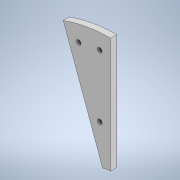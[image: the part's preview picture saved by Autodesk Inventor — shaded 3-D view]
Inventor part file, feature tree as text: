
AUTODESK INVENTOR PART (.ipt)
format: ipt  version: 2020.3 (Build 243373000, 373)  size: 159,232 bytes
history: native  units: mm
features: extrude x4, sketch x3, pattern_circular x1
ambient origin geometry x8: Origin, YZ Plane, XZ Plane, XY Plane, X Axis, Y Axis, Z Axis, Center Point
bodies: Solid1 (feature_tree)
feature tree (8):
  extrude  "Extrusion1"  Depth=90.0mm
  extrude  "Extrusion2"  Depth=4.0mm
  pattern_circular  "Circular Pattern1"  Count=8  [1 undecoded]
  extrude  "Extrusion4"  TaperAngle=15.0deg  [1 undecoded]
  extrude  "Extrusion5"  Depth=10.0mm TaperAngle=0.0deg
  sketch  "Sketch2"  dims[d0=120.0deg d2=90.0mm]
  sketch  "Sketch4"  dims[d3=4.0mm d4=0.0mm d5=3.0mm]
  sketch  "Sketch5"  dims[d6=3.0mm d7=80.0mm d9=15.0deg d11=10.0mm d12=0.0mm d13=120.0mm d14=38.397244mm d16=80.0mm d17=3.0mm d18=0.872665mm d27=0.872665mm d28=40.0mm d29=30.0mm d30=10.0mm d31=0.0mm d32=3.490659mm d33=10.0mm d34=0.0mm]
note: 2 required parameter values undecoded (feature->parameter linkage not recoverable at this tier; creation-order binding heuristic only, values carry confidence <= 0.55)
